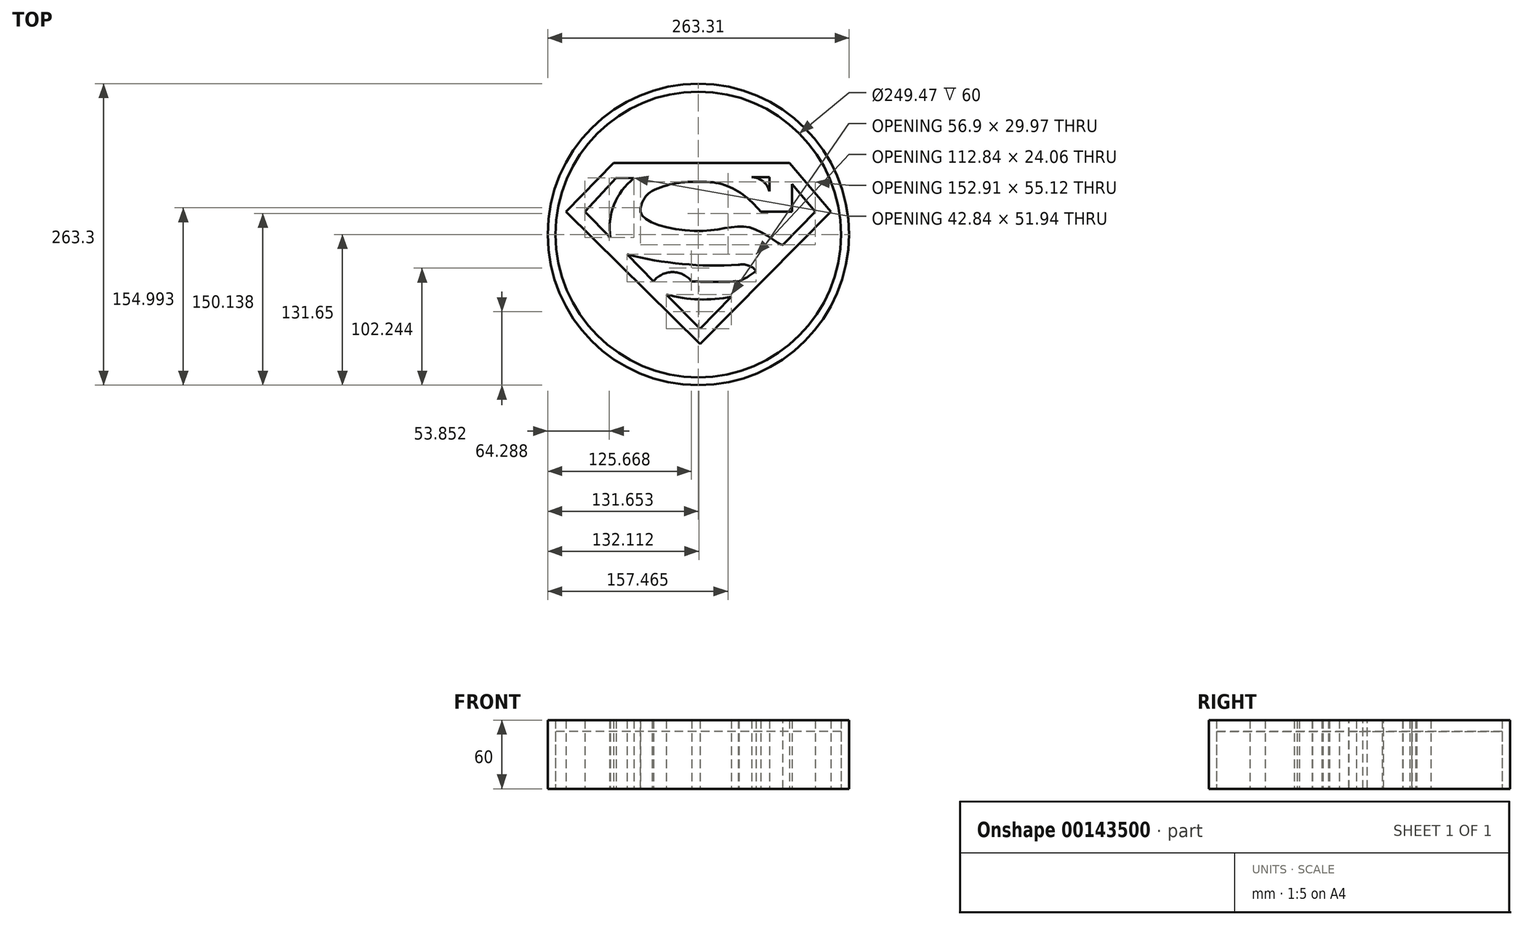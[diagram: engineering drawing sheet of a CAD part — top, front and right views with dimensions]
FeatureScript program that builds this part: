
annotation { "Feature Type Name" : "Feature", "Feature Type Description" : "" }
export const myFeature = defineFeature(function(context is Context, id is Id, definition is map)
    precondition{}
    {
        {
            var Q0;
            Q0=qCreatedBy(makeId("Top.planeOp"),FACE);
            var sketch = newSketch(context, id + "F0", { "sketchPlane" : qUnion([Q0])});
            skLineSegment(sketch, "E0", {"start": v(-78.84, 62.36) * mm, "end": v(74.93, 62.36) * mm});
            skLineSegment(sketch, "E1", {"start": v(-120.53, 20.07) * mm, "end": v(-78.84, 62.36) * mm});
            skLineSegment(sketch, "E2", {"start": v(-120.53, 20.07) * mm, "end": v(-3.29, -95.58) * mm});
            skLineSegment(sketch, "E3", {"start": v(74.93, 62.36) * mm, "end": v(111, 20.07) * mm});
            skLineSegment(sketch, "E4", {"start": v(111, 20.07) * mm, "end": v(-3.29, -95.58) * mm});
            skLineSegment(sketch, "E5", {"start": v(76.99, 44.12) * mm, "end": v(97.5, 20.07) * mm});
            skLineSegment(sketch, "E6", {"start": v(76.99, 44.12) * mm, "end": v(76.99, 20.07) * mm});
            skLineSegment(sketch, "E7", {"start": v(76.99, 20.07) * mm, "end": v(49.85, 20.07) * mm});
            skLineSegment(sketch, "E8", {"start": v(-103.99, 20.07) * mm, "end": v(-76.5, 49.31) * mm});
            skPoint(sketch, "E9", {"position": v(-3.29, 45.8) * mm});
            skPoint(sketch, "E10", {"position": v(-55.4, 20.07) * mm});
            skPoint(sketch, "E11", {"position": v(43.36, 5.17) * mm});
            skFitSpline(sketch, "E12", {"points": [v(49.85, 20.07) * mm, v(-3.29, 45.8) * mm, v(-55.4, 20.07) * mm, v(-3.29, 3.01) * mm, v(43.36, 5.17) * mm, v(68.82, -9.07) * mm, v(49.85, 20.07) * mm]});
            skPoint(sketch, "E13", {"position": v(24.63, 6.44) * mm});
            skLineSegment(sketch, "E14", {"start": v(41.76, 50.01) * mm, "end": v(57.24, 50.01) * mm});
            skLineSegment(sketch, "E15", {"start": v(57.24, 50.01) * mm, "end": v(57.24, 37.62) * mm});
            skArc(sketch, "E16", {"start": v(57.24, 37.62) * mm, "mid": v(51.67, 46.53) * mm, "end": v(41.76, 50.01) * mm});
            skLineSegment(sketch, "E17", {"start": v(-3.29, -82.35) * mm, "end": v(24.14, -54.47) * mm});
            skLineSegment(sketch, "E18", {"start": v(-103.99, 20.07) * mm, "end": v(-81.68, -2.63) * mm});
            skPoint(sketch, "E19", {"position": v(-44.06, -40.89) * mm});
            skPoint(sketch, "E20", {"position": v(30.62, -40.89) * mm});
            skPoint(sketch, "E21", {"position": v(45.67, -32.6) * mm});
            skPoint(sketch, "E22", {"position": v(-53.64, -31.14) * mm});
            skArc(sketch, "E23", {"start": v(-10.57, -40.89) * mm, "mid": v(-27.31, -32.91) * mm, "end": v(-44.06, -40.89) * mm});
            skPoint(sketch, "E24", {"position": v(-32.76, -52.38) * mm});
            skPoint(sketch, "E25", {"position": v(24.14, -54.47) * mm});
            skArc(sketch, "E26", {"start": v(-32.76, -52.38) * mm, "mid": v(-4.43, -56.7) * mm, "end": v(24.14, -54.47) * mm});
            skLineSegment(sketch, "E27.trimOffspring", {"start": v(-32.76, -52.38) * mm, "end": v(-3.29, -82.35) * mm});
            skPoint(sketch, "E28", {"position": v(30.05, -26.56) * mm});
            skArc(sketch, "E29", {"start": v(-10.57, -40.89) * mm, "mid": v(10.02, -41.44) * mm, "end": v(30.62, -40.89) * mm});
            skArc(sketch, "E30", {"start": v(-67.17, -17.37) * mm, "mid": v(-18.92, -25.72) * mm, "end": v(30.05, -26.56) * mm});
            skLineSegment(sketch, "E31.trimOffspring", {"start": v(68.82, -9.07) * mm, "end": v(97.5, 20.07) * mm});
            skLineSegment(sketch, "E32.trimOffspring", {"start": v(-67.17, -17.37) * mm, "end": v(-44.06, -40.89) * mm});
            skPoint(sketch, "E33", {"position": v(45.67, -31.67) * mm});
            skArc(sketch, "E34", {"start": v(30.62, -40.89) * mm, "mid": v(38.5, -36.86) * mm, "end": v(45.67, -31.67) * mm});
            skArc(sketch, "E35", {"start": v(45.67, -31.67) * mm, "mid": v(38.57, -26.97) * mm, "end": v(30.05, -26.56) * mm});
            skPoint(sketch, "E36", {"position": v(-61.15, 49.02) * mm});
            skArc(sketch, "E37", {"start": v(-61.15, 49.02) * mm, "mid": v(-78.44, 26) * mm, "end": v(-81.68, -2.63) * mm});
            skLineSegment(sketch, "E38", {"start": v(-76.5, 49.31) * mm, "end": v(-61.15, 49.02) * mm});
            skPoint(sketch, "E39", {"position": v(-45.06, 38.17) * mm});
            skArc(sketch, "E40", {"start": v(-3.29, 45.8) * mm, "mid": v(-24.67, 44.7) * mm, "end": v(-45.06, 38.17) * mm});
            skArc(sketch, "E41", {"start": v(-45.06, 38.17) * mm, "mid": v(-52.59, 30.47) * mm, "end": v(-55.4, 20.07) * mm});
            skSolve(sketch);
        }
        {
            var Q0;
            Q0=makeQuery(id+"F0.imprint","IMPRINT",FACE,{"disambiguationData":[TD([[makeQuery(id+"F0.imprint","IMPRINT",EDGE,{"derivedFrom":sQuery(id+"F0.wireOp",EDGE,"E0")}),-1.0]])]});
            extrude(context, id + "F1", {"entities" : qUnion([Q0]), "depth" : 60 * mm});
        }
        {
            var Q0;
            Q0=qCreatedBy(makeId("Top.planeOp"),FACE);
            var sketch = newSketch(context, id + "F2", { "sketchPlane" : qUnion([Q0])});
            skCircle(sketch, "E42", {"center": v(-4.77, 0) * mm, "radius": 124.73 * mm});
            skCircle(sketch, "E43", {"center": v(-4.77, 0) * mm, "radius": 131.65 * mm});
            skSolve(sketch);
        }
        {
            var Q0;
            Q0=makeQuery(id+"F2.imprint","IMPRINT",FACE,{"disambiguationData":[TD([[makeQuery(id+"F2.imprint","IMPRINT",EDGE,{"derivedFrom":sQuery(id+"F2.wireOp",EDGE,"E42")}),-1.0]])]});
            extrude(context, id + "F3", {"entities" : qUnion([Q0]), "depth" : 60 * mm});
        }
        {
            var Q0;
            Q0=makeQuery(id+"F2.imprint","IMPRINT",FACE,{"disambiguationData":[TD([[makeQuery(id+"F2.imprint","IMPRINT",EDGE,{"derivedFrom":sQuery(id+"F2.wireOp",EDGE,"E42")}),1.0]])]});
            extrude(context, id + "F4", {"entities" : qUnion([Q0]), "depth" : 50 * mm});
        }
    });
